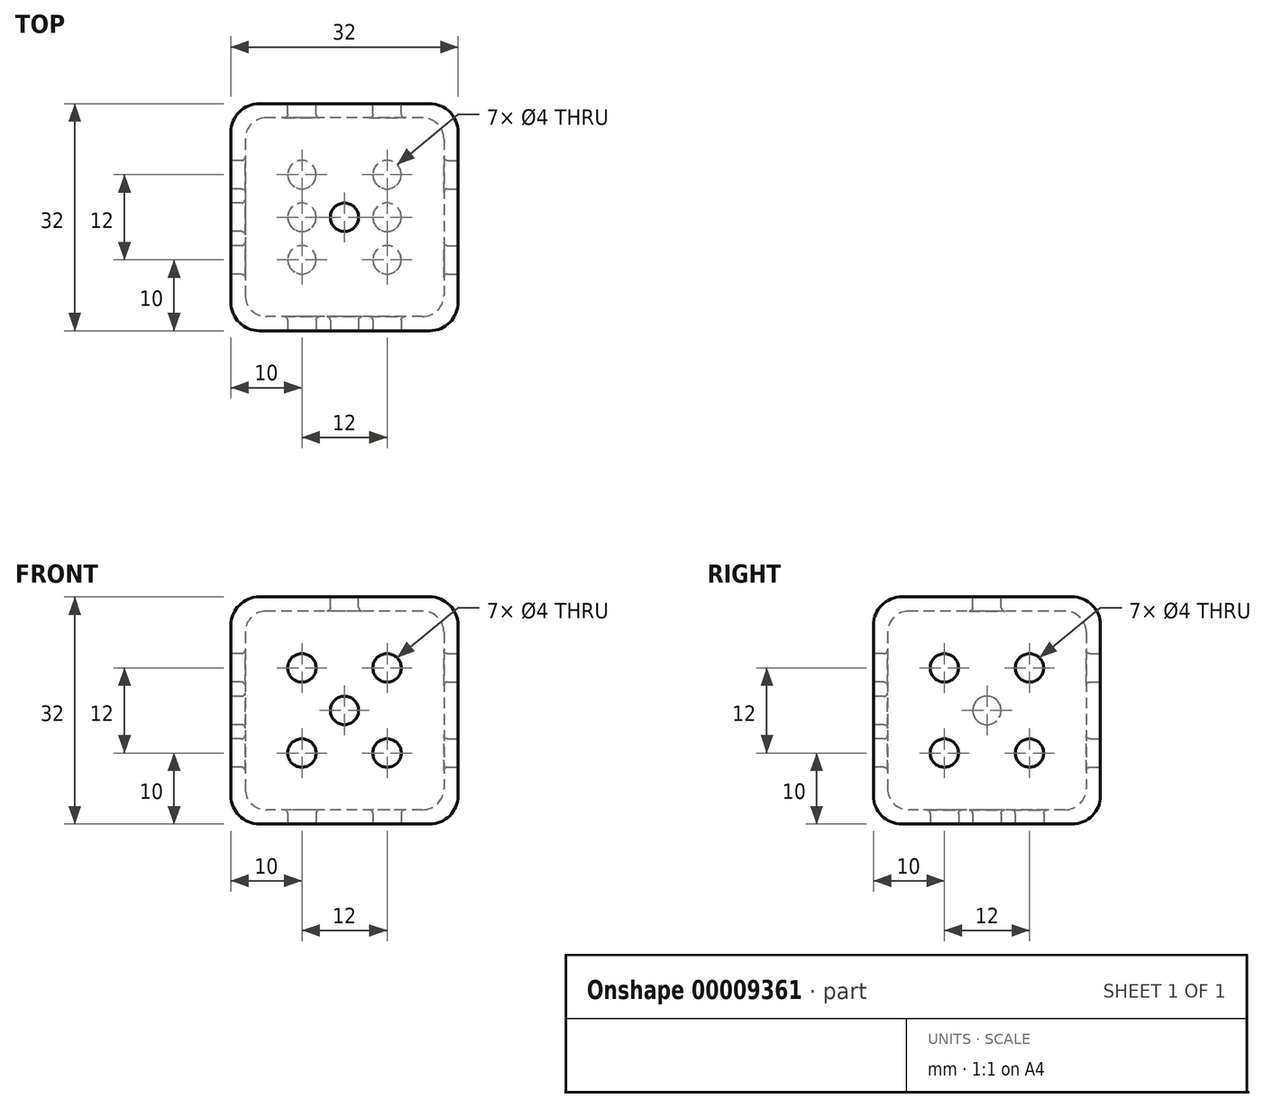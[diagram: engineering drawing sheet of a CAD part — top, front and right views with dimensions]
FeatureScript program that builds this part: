
annotation { "Feature Type Name" : "Feature", "Feature Type Description" : "" }
export const myFeature = defineFeature(function(context is Context, id is Id, definition is map)
    precondition{}
    {
        {
            var Q0;
            Q0=qCreatedBy(makeId("Top.planeOp"),FACE);
            var sketch = newSketch(context, id + "F0", { "sketchPlane" : qUnion([Q0])});
            skLineSegment(sketch, "E0.rect.bottom", {"start": v(16, 16) * mm, "end": v(-16, 16) * mm});
            skLineSegment(sketch, "E0.rect.top", {"start": v(16, -16) * mm, "end": v(-16, -16) * mm});
            skLineSegment(sketch, "E0.rect.left", {"start": v(16, 16) * mm, "end": v(16, -16) * mm});
            skLineSegment(sketch, "E0.rect.right", {"start": v(-16, 16) * mm, "end": v(-16, -16) * mm});
            skPoint(sketch, "E0.rect.middle", {"position": v(0, 0) * mm});
            skSolve(sketch);
        }
        {
            var Q0;
            Q0=makeQuery(id+"F0.imprint","IMPRINT",FACE,{"disambiguationData":[TD([[makeQuery(id+"F0.imprint","IMPRINT",EDGE,{"derivedFrom":sQuery(id+"F0.wireOp",EDGE,"E0.rect.bottom")}),1.0]])]});
            extrude(context, id + "F1", {"entities" : qUnion([Q0]), "depth" : 32 * mm});
        }
        {
            var Q0;
            Q0=qCreatedBy(makeId("Top.planeOp"),FACE);
            cPlane(context, id + "F2", {"entities" : qUnion([Q0]), "cplaneType" : CPlaneType.OFFSET, "offset" : 2 * mm, "width" : 150 * mm, "height" : 150 * mm});
        }
        {
            var Q0;
            Q0=qCreatedBy(id+"F2.planeOp",FACE);
            var sketch = newSketch(context, id + "F3", { "sketchPlane" : qUnion([Q0])});
            skLineSegment(sketch, "E1.rect.bottom", {"start": v(14, 14) * mm, "end": v(-14, 14) * mm});
            skLineSegment(sketch, "E1.rect.top", {"start": v(14, -14) * mm, "end": v(-14, -14) * mm});
            skLineSegment(sketch, "E1.rect.left", {"start": v(14, 14) * mm, "end": v(14, -14) * mm});
            skLineSegment(sketch, "E1.rect.right", {"start": v(-14, 14) * mm, "end": v(-14, -14) * mm});
            skPoint(sketch, "E1.rect.middle", {"position": v(0, 0) * mm});
            skSolve(sketch);
        }
        {
            var Q0;
            Q0 = qSketchRegion(id + "F3", true);
            extrude(context, id + "F4", {"entities" : qUnion([Q0]), "operationType" : NewBodyOperationType.REMOVE, "depth" : 28 * mm});
        }
        {
            var Q0;
            Q0=makeQuery(id+"F4.boolean.opBoolean","COPY",EDGE,{"derivedFrom":makeQuery(id+"F4.opExtrude","SWEPT_EDGE",EDGE,{"disambiguationData":[OSD([sQuery(id+"F3.wireOp",EDGE,"E1.rect.bottom"),sQuery(id+"F3.wireOp",EDGE,"E1.rect.left")])]})});
            var Q1;
            Q1=makeQuery(id+"F4.boolean.opBoolean","COPY",EDGE,{"derivedFrom":makeQuery(id+"F4.opExtrude","CAP_EDGE",EDGE,{"disambiguationData":[OSD([sQuery(id+"F3.wireOp",EDGE,"E1.rect.bottom")])],"isStart":false})});
            var Q2;
            Q2=makeQuery(id+"F4.boolean.opBoolean","COPY",EDGE,{"derivedFrom":makeQuery(id+"F4.opExtrude","CAP_EDGE",EDGE,{"disambiguationData":[OSD([sQuery(id+"F3.wireOp",EDGE,"E1.rect.left")])],"isStart":false})});
            var Q3;
            Q3=makeQuery(id+"F4.boolean.opBoolean","COPY",EDGE,{"derivedFrom":makeQuery(id+"F4.opExtrude","CAP_EDGE",EDGE,{"disambiguationData":[OSD([sQuery(id+"F3.wireOp",EDGE,"E1.rect.right")])],"isStart":false})});
            var Q4;
            Q4=makeQuery(id+"F4.boolean.opBoolean","COPY",EDGE,{"derivedFrom":makeQuery(id+"F4.opExtrude","SWEPT_EDGE",EDGE,{"disambiguationData":[OSD([sQuery(id+"F3.wireOp",EDGE,"E1.rect.bottom"),sQuery(id+"F3.wireOp",EDGE,"E1.rect.right")])]})});
            var Q5;
            Q5=makeQuery(id+"F4.boolean.opBoolean","COPY",EDGE,{"derivedFrom":makeQuery(id+"F4.opExtrude","CAP_EDGE",EDGE,{"disambiguationData":[OSD([sQuery(id+"F3.wireOp",EDGE,"E1.rect.bottom")])],"isStart":true})});
            var Q6;
            Q6=makeQuery(id+"F4.boolean.opBoolean","COPY",EDGE,{"derivedFrom":makeQuery(id+"F4.opExtrude","CAP_EDGE",EDGE,{"disambiguationData":[OSD([sQuery(id+"F3.wireOp",EDGE,"E1.rect.right")])],"isStart":true})});
            var Q7;
            Q7=makeQuery(id+"F4.boolean.opBoolean","COPY",EDGE,{"derivedFrom":makeQuery(id+"F4.opExtrude","CAP_EDGE",EDGE,{"disambiguationData":[OSD([sQuery(id+"F3.wireOp",EDGE,"E1.rect.left")])],"isStart":true})});
            var Q8;
            Q8=makeQuery(id+"F4.boolean.opBoolean","COPY",EDGE,{"derivedFrom":makeQuery(id+"F4.opExtrude","CAP_EDGE",EDGE,{"disambiguationData":[OSD([sQuery(id+"F3.wireOp",EDGE,"E1.rect.top")])],"isStart":true})});
            var Q9;
            Q9=makeQuery(id+"F4.boolean.opBoolean","COPY",EDGE,{"derivedFrom":makeQuery(id+"F4.opExtrude","SWEPT_EDGE",EDGE,{"disambiguationData":[OSD([sQuery(id+"F3.wireOp",EDGE,"E1.rect.top"),sQuery(id+"F3.wireOp",EDGE,"E1.rect.right")])]})});
            var Q10;
            Q10=makeQuery(id+"F4.boolean.opBoolean","COPY",EDGE,{"derivedFrom":makeQuery(id+"F4.opExtrude","SWEPT_EDGE",EDGE,{"disambiguationData":[OSD([sQuery(id+"F3.wireOp",EDGE,"E1.rect.top"),sQuery(id+"F3.wireOp",EDGE,"E1.rect.left")])]})});
            var Q11;
            Q11=makeQuery(id+"F4.boolean.opBoolean","COPY",EDGE,{"derivedFrom":makeQuery(id+"F4.opExtrude","CAP_EDGE",EDGE,{"disambiguationData":[OSD([sQuery(id+"F3.wireOp",EDGE,"E1.rect.top")])],"isStart":false})});
            fillet(context, id + "F5", {"entities" : qUnion([Q0, Q1, Q2, Q3, Q4, Q5, Q6, Q7, Q8, Q9, Q10, Q11]), "radius" : 3 * mm, "tangentPropagation" : true, "allowEdgeOverflow" : false});
        }
        {
            var Q0;
            Q0=makeQuery(id+"F1.opExtrude","SWEPT_EDGE",EDGE,{"disambiguationData":[OSD([sQuery(id+"F0.wireOp",EDGE,"E0.rect.bottom"),sQuery(id+"F0.wireOp",EDGE,"E0.rect.left")])]});
            var Q1;
            Q1=makeQuery(id+"F1.opExtrude","CAP_EDGE",EDGE,{"disambiguationData":[OSD([sQuery(id+"F0.wireOp",EDGE,"E0.rect.bottom")])],"isStart":false});
            var Q2;
            Q2=makeQuery(id+"F1.opExtrude","CAP_EDGE",EDGE,{"disambiguationData":[OSD([sQuery(id+"F0.wireOp",EDGE,"E0.rect.bottom")])],"isStart":true});
            var Q3;
            Q3=makeQuery(id+"F1.opExtrude","SWEPT_EDGE",EDGE,{"disambiguationData":[OSD([sQuery(id+"F0.wireOp",EDGE,"E0.rect.bottom"),sQuery(id+"F0.wireOp",EDGE,"E0.rect.right")])]});
            var Q4;
            Q4=makeQuery(id+"F1.opExtrude","CAP_EDGE",EDGE,{"disambiguationData":[OSD([sQuery(id+"F0.wireOp",EDGE,"E0.rect.right")])],"isStart":false});
            var Q5;
            Q5=makeQuery(id+"F1.opExtrude","CAP_EDGE",EDGE,{"disambiguationData":[OSD([sQuery(id+"F0.wireOp",EDGE,"E0.rect.left")])],"isStart":false});
            var Q6;
            Q6=makeQuery(id+"F1.opExtrude","CAP_EDGE",EDGE,{"disambiguationData":[OSD([sQuery(id+"F0.wireOp",EDGE,"E0.rect.left")])],"isStart":true});
            var Q7;
            Q7=makeQuery(id+"F1.opExtrude","SWEPT_EDGE",EDGE,{"disambiguationData":[OSD([sQuery(id+"F0.wireOp",EDGE,"E0.rect.top"),sQuery(id+"F0.wireOp",EDGE,"E0.rect.left")])]});
            var Q8;
            Q8=makeQuery(id+"F1.opExtrude","CAP_EDGE",EDGE,{"disambiguationData":[OSD([sQuery(id+"F0.wireOp",EDGE,"E0.rect.top")])],"isStart":false});
            var Q9;
            Q9=makeQuery(id+"F1.opExtrude","SWEPT_EDGE",EDGE,{"disambiguationData":[OSD([sQuery(id+"F0.wireOp",EDGE,"E0.rect.top"),sQuery(id+"F0.wireOp",EDGE,"E0.rect.right")])]});
            var Q10;
            Q10=makeQuery(id+"F1.opExtrude","CAP_EDGE",EDGE,{"disambiguationData":[OSD([sQuery(id+"F0.wireOp",EDGE,"E0.rect.top")])],"isStart":true});
            var Q11;
            Q11=makeQuery(id+"F1.opExtrude","CAP_EDGE",EDGE,{"disambiguationData":[OSD([sQuery(id+"F0.wireOp",EDGE,"E0.rect.right")])],"isStart":true});
            fillet(context, id + "F6", {"entities" : qUnion([Q0, Q1, Q2, Q3, Q4, Q5, Q6, Q7, Q8, Q9, Q10, Q11]), "radius" : 4 * mm, "tangentPropagation" : true, "allowEdgeOverflow" : false});
        }
        {
            var Q0;
            Q0=makeQuery(id+"F1.opExtrude","CAP_FACE",FACE,{"disambiguationData":[OSD([sQuery(id+"F0.wireOp",EDGE,"E0.rect.bottom"),sQuery(id+"F0.wireOp",EDGE,"E0.rect.top"),sQuery(id+"F0.wireOp",EDGE,"E0.rect.left"),sQuery(id+"F0.wireOp",EDGE,"E0.rect.right")])],"isStart":false});
            var sketch = newSketch(context, id + "F7", { "sketchPlane" : qUnion([Q0])});
            skCircle(sketch, "E2", {"center": v(0, 0) * mm, "radius": 2 * mm});
            skSolve(sketch);
        }
        {
            var Q0;
            Q0 = qSketchRegion(id + "F7", true);
            extrude(context, id + "F8", {"entities" : qUnion([Q0]), "operationType" : NewBodyOperationType.REMOVE, "oppositeDirection" : true, "depth" : 5 * mm});
        }
        {
            var Q0;
            Q0=makeQuery(id+"F1.opExtrude","SWEPT_FACE",FACE,{"disambiguationData":[OSD([sQuery(id+"F0.wireOp",EDGE,"E0.rect.bottom")])]});
            var sketch = newSketch(context, id + "F9", { "sketchPlane" : qUnion([Q0])});
            skLineSegment(sketch, "E3", {"start": v(12, 28) * mm, "end": v(-12, 4) * mm, "construction": true});
            skPoint(sketch, "E4", {"position": v(0, 16) * mm});
            skPoint(sketch, "E5", {"position": v(0, 28) * mm});
            skPoint(sketch, "E6", {"position": v(12, 16) * mm});
            skPoint(sketch, "E7", {"position": v(0, 4) * mm});
            skPoint(sketch, "E8", {"position": v(-12, 16) * mm});
            skLineSegment(sketch, "E9", {"start": v(0, 28) * mm, "end": v(12, 16) * mm, "construction": true});
            skLineSegment(sketch, "E10", {"start": v(-12, 16) * mm, "end": v(0, 4) * mm, "construction": true});
            skCircle(sketch, "E11", {"center": v(6, 22) * mm, "radius": 2 * mm});
            skCircle(sketch, "E12", {"center": v(-6, 10) * mm, "radius": 2 * mm});
            skSolve(sketch);
        }
        {
            var Q0;
            Q0 = qSketchRegion(id + "F9", true);
            extrude(context, id + "F10", {"entities" : qUnion([Q0]), "operationType" : NewBodyOperationType.REMOVE, "oppositeDirection" : true, "depth" : 5 * mm});
        }
        {
            var Q0;
            Q0=makeQuery(id+"F1.opExtrude","SWEPT_FACE",FACE,{"disambiguationData":[OSD([sQuery(id+"F0.wireOp",EDGE,"E0.rect.right")])]});
            var sketch = newSketch(context, id + "F11", { "sketchPlane" : qUnion([Q0])});
            skLineSegment(sketch, "E13", {"start": v(-12, 28) * mm, "end": v(12, 4) * mm, "construction": true});
            skLineSegment(sketch, "E14", {"start": v(12, 4) * mm, "end": v(0, 16) * mm, "construction": true});
            skLineSegment(sketch, "E15", {"start": v(0, 16) * mm, "end": v(-12, 28) * mm, "construction": true});
            skCircle(sketch, "E16", {"center": v(-6, 22) * mm, "radius": 2 * mm});
            skCircle(sketch, "E17", {"center": v(0, 16) * mm, "radius": 2 * mm});
            skCircle(sketch, "E18", {"center": v(6, 10) * mm, "radius": 2 * mm});
            skSolve(sketch);
        }
        {
            var Q0;
            Q0 = qSketchRegion(id + "F11", true);
            extrude(context, id + "F12", {"entities" : qUnion([Q0]), "operationType" : NewBodyOperationType.REMOVE, "oppositeDirection" : true, "depth" : 5 * mm});
        }
        {
            var Q0;
            Q0=makeQuery(id+"F1.opExtrude","SWEPT_FACE",FACE,{"disambiguationData":[OSD([sQuery(id+"F0.wireOp",EDGE,"E0.rect.left")])]});
            var sketch = newSketch(context, id + "F13", { "sketchPlane" : qUnion([Q0])});
            skLineSegment(sketch, "E19", {"start": v(-12, 16) * mm, "end": v(0, 28) * mm, "construction": true});
            skLineSegment(sketch, "E20", {"start": v(0, 28) * mm, "end": v(12, 16) * mm, "construction": true});
            skLineSegment(sketch, "E21", {"start": v(12, 16) * mm, "end": v(0, 4) * mm, "construction": true});
            skLineSegment(sketch, "E22", {"start": v(0, 4) * mm, "end": v(-12, 16) * mm, "construction": true});
            skCircle(sketch, "E23", {"center": v(-6, 10) * mm, "radius": 2 * mm});
            skCircle(sketch, "E24", {"center": v(-6, 22) * mm, "radius": 2 * mm});
            skCircle(sketch, "E25", {"center": v(6, 22) * mm, "radius": 2 * mm});
            skCircle(sketch, "E26", {"center": v(6, 10) * mm, "radius": 2 * mm});
            skSolve(sketch);
        }
        {
            var Q0;
            Q0 = qSketchRegion(id + "F13", true);
            extrude(context, id + "F14", {"entities" : qUnion([Q0]), "operationType" : NewBodyOperationType.REMOVE, "oppositeDirection" : true, "depth" : 5 * mm});
        }
        {
            var Q0;
            Q0=makeQuery(id+"F1.opExtrude","SWEPT_FACE",FACE,{"disambiguationData":[OSD([sQuery(id+"F0.wireOp",EDGE,"E0.rect.top")])]});
            var sketch = newSketch(context, id + "F15", { "sketchPlane" : qUnion([Q0])});
            skLineSegment(sketch, "E27", {"start": v(0, 28) * mm, "end": v(12, 16) * mm, "construction": true});
            skLineSegment(sketch, "E28", {"start": v(12, 16) * mm, "end": v(0, 4) * mm, "construction": true});
            skLineSegment(sketch, "E29", {"start": v(0, 4) * mm, "end": v(-12, 16) * mm, "construction": true});
            skLineSegment(sketch, "E30", {"start": v(-12, 16) * mm, "end": v(0, 28) * mm, "construction": true});
            skLineSegment(sketch, "E31", {"start": v(-12, 16) * mm, "end": v(12, 16) * mm, "construction": true});
            skCircle(sketch, "E32", {"center": v(-6, 22) * mm, "radius": 2 * mm});
            skCircle(sketch, "E33", {"center": v(6, 22) * mm, "radius": 2 * mm});
            skCircle(sketch, "E34", {"center": v(6, 10) * mm, "radius": 2 * mm});
            skCircle(sketch, "E35", {"center": v(-6, 10) * mm, "radius": 2 * mm});
            skCircle(sketch, "E36", {"center": v(0, 16) * mm, "radius": 2 * mm});
            skSolve(sketch);
        }
        {
            var Q0;
            Q0 = qSketchRegion(id + "F15", true);
            extrude(context, id + "F16", {"entities" : qUnion([Q0]), "operationType" : NewBodyOperationType.REMOVE, "oppositeDirection" : true, "depth" : 5 * mm});
        }
        {
            var Q0;
            Q0=makeQuery(id+"F1.opExtrude","CAP_FACE",FACE,{"disambiguationData":[OSD([sQuery(id+"F0.wireOp",EDGE,"E0.rect.bottom"),sQuery(id+"F0.wireOp",EDGE,"E0.rect.top"),sQuery(id+"F0.wireOp",EDGE,"E0.rect.left"),sQuery(id+"F0.wireOp",EDGE,"E0.rect.right")])],"isStart":true});
            var sketch = newSketch(context, id + "F17", { "sketchPlane" : qUnion([Q0])});
            skLineSegment(sketch, "E37", {"start": v(0, 12) * mm, "end": v(-12, 0) * mm, "construction": true});
            skLineSegment(sketch, "E38", {"start": v(-12, 0) * mm, "end": v(0, -12) * mm, "construction": true});
            skLineSegment(sketch, "E39", {"start": v(0, -12) * mm, "end": v(12, 0) * mm, "construction": true});
            skLineSegment(sketch, "E40", {"start": v(12, 0) * mm, "end": v(0, 12) * mm, "construction": true});
            skLineSegment(sketch, "E41", {"start": v(6, 6) * mm, "end": v(6, -6) * mm, "construction": true});
            skLineSegment(sketch, "E42", {"start": v(6, -6) * mm, "end": v(-6, -6) * mm, "construction": true});
            skLineSegment(sketch, "E43", {"start": v(-6, -6) * mm, "end": v(-6, 6) * mm, "construction": true});
            skLineSegment(sketch, "E44", {"start": v(-6, 6) * mm, "end": v(6, 6) * mm, "construction": true});
            skCircle(sketch, "E45", {"center": v(-6, 6) * mm, "radius": 2 * mm});
            skCircle(sketch, "E46", {"center": v(-6, 0) * mm, "radius": 2 * mm});
            skCircle(sketch, "E47", {"center": v(-6, -6) * mm, "radius": 2 * mm});
            skCircle(sketch, "E48", {"center": v(6, -6) * mm, "radius": 2 * mm});
            skCircle(sketch, "E49", {"center": v(6, 0) * mm, "radius": 2 * mm});
            skCircle(sketch, "E50", {"center": v(6, 6) * mm, "radius": 2 * mm});
            skSolve(sketch);
        }
        {
            var Q0;
            Q0 = qSketchRegion(id + "F17", true);
            extrude(context, id + "F18", {"entities" : qUnion([Q0]), "operationType" : NewBodyOperationType.REMOVE, "oppositeDirection" : true, "depth" : 5 * mm});
        }
        {
            var Q0;
            Q0=makeQuery(id+"F8.boolean.opBoolean","COPY",EDGE,{"derivedFrom":makeQuery(id+"F8.opExtrude","CAP_EDGE",EDGE,{"disambiguationData":[OSD([sQuery(id+"F7.wireOp",EDGE,"E2")])],"isStart":true})});
            var Q1;
            Q1=makeQuery(id+"F8.boolean.opBoolean","INTERSECT",EDGE,{"derivedFrom":[makeQuery(id+"F4.boolean.opBoolean","COPY",FACE,{"derivedFrom":makeQuery(id+"F4.opExtrude","CAP_FACE",FACE,{"disambiguationData":[OSD([sQuery(id+"F3.wireOp",EDGE,"E1.rect.bottom"),sQuery(id+"F3.wireOp",EDGE,"E1.rect.top"),sQuery(id+"F3.wireOp",EDGE,"E1.rect.left"),sQuery(id+"F3.wireOp",EDGE,"E1.rect.right")])],"isStart":false})}),makeQuery(id+"F8.opExtrude","SWEPT_FACE",FACE,{"disambiguationData":[OSD([sQuery(id+"F7.wireOp",EDGE,"E2")])]})]});
            var Q2;
            Q2=makeQuery(id+"F10.boolean.opBoolean","COPY",EDGE,{"derivedFrom":makeQuery(id+"F10.opExtrude","CAP_EDGE",EDGE,{"disambiguationData":[OSD([sQuery(id+"F9.wireOp",EDGE,"E11")])],"isStart":true})});
            var Q3;
            Q3=makeQuery(id+"F10.boolean.opBoolean","COPY",EDGE,{"derivedFrom":makeQuery(id+"F10.opExtrude","CAP_EDGE",EDGE,{"disambiguationData":[OSD([sQuery(id+"F9.wireOp",EDGE,"E12")])],"isStart":true})});
            var Q4;
            Q4=makeQuery(id+"F10.boolean.opBoolean","INTERSECT",EDGE,{"derivedFrom":[makeQuery(id+"F4.boolean.opBoolean","COPY",FACE,{"derivedFrom":makeQuery(id+"F4.opExtrude","SWEPT_FACE",FACE,{"disambiguationData":[OSD([sQuery(id+"F3.wireOp",EDGE,"E1.rect.bottom")])]})}),makeQuery(id+"F10.opExtrude","SWEPT_FACE",FACE,{"disambiguationData":[OSD([sQuery(id+"F9.wireOp",EDGE,"E11")])]})]});
            var Q5;
            Q5=makeQuery(id+"F10.boolean.opBoolean","INTERSECT",EDGE,{"derivedFrom":[makeQuery(id+"F4.boolean.opBoolean","COPY",FACE,{"derivedFrom":makeQuery(id+"F4.opExtrude","SWEPT_FACE",FACE,{"disambiguationData":[OSD([sQuery(id+"F3.wireOp",EDGE,"E1.rect.bottom")])]})}),makeQuery(id+"F10.opExtrude","SWEPT_FACE",FACE,{"disambiguationData":[OSD([sQuery(id+"F9.wireOp",EDGE,"E12")])]})]});
            var Q6;
            Q6=makeQuery(id+"F12.boolean.opBoolean","INTERSECT",EDGE,{"derivedFrom":[makeQuery(id+"F4.boolean.opBoolean","COPY",FACE,{"derivedFrom":makeQuery(id+"F4.opExtrude","SWEPT_FACE",FACE,{"disambiguationData":[OSD([sQuery(id+"F3.wireOp",EDGE,"E1.rect.right")])]})}),makeQuery(id+"F12.opExtrude","SWEPT_FACE",FACE,{"disambiguationData":[OSD([sQuery(id+"F11.wireOp",EDGE,"E16")])]})]});
            var Q7;
            Q7=makeQuery(id+"F12.boolean.opBoolean","COPY",EDGE,{"derivedFrom":makeQuery(id+"F12.opExtrude","CAP_EDGE",EDGE,{"disambiguationData":[OSD([sQuery(id+"F11.wireOp",EDGE,"E16")])],"isStart":true})});
            var Q8;
            Q8=makeQuery(id+"F12.boolean.opBoolean","INTERSECT",EDGE,{"derivedFrom":[makeQuery(id+"F4.boolean.opBoolean","COPY",FACE,{"derivedFrom":makeQuery(id+"F4.opExtrude","SWEPT_FACE",FACE,{"disambiguationData":[OSD([sQuery(id+"F3.wireOp",EDGE,"E1.rect.right")])]})}),makeQuery(id+"F12.opExtrude","SWEPT_FACE",FACE,{"disambiguationData":[OSD([sQuery(id+"F11.wireOp",EDGE,"E17")])]})]});
            var Q9;
            Q9=makeQuery(id+"F12.boolean.opBoolean","COPY",EDGE,{"derivedFrom":makeQuery(id+"F12.opExtrude","CAP_EDGE",EDGE,{"disambiguationData":[OSD([sQuery(id+"F11.wireOp",EDGE,"E17")])],"isStart":true})});
            var Q10;
            Q10=makeQuery(id+"F12.boolean.opBoolean","INTERSECT",EDGE,{"derivedFrom":[makeQuery(id+"F4.boolean.opBoolean","COPY",FACE,{"derivedFrom":makeQuery(id+"F4.opExtrude","SWEPT_FACE",FACE,{"disambiguationData":[OSD([sQuery(id+"F3.wireOp",EDGE,"E1.rect.right")])]})}),makeQuery(id+"F12.opExtrude","SWEPT_FACE",FACE,{"disambiguationData":[OSD([sQuery(id+"F11.wireOp",EDGE,"E18")])]})]});
            var Q11;
            Q11=makeQuery(id+"F12.boolean.opBoolean","COPY",EDGE,{"derivedFrom":makeQuery(id+"F12.opExtrude","CAP_EDGE",EDGE,{"disambiguationData":[OSD([sQuery(id+"F11.wireOp",EDGE,"E18")])],"isStart":true})});
            var Q12;
            Q12=makeQuery(id+"F14.boolean.opBoolean","INTERSECT",EDGE,{"derivedFrom":[makeQuery(id+"F4.boolean.opBoolean","COPY",FACE,{"derivedFrom":makeQuery(id+"F4.opExtrude","SWEPT_FACE",FACE,{"disambiguationData":[OSD([sQuery(id+"F3.wireOp",EDGE,"E1.rect.left")])]})}),makeQuery(id+"F14.opExtrude","SWEPT_FACE",FACE,{"disambiguationData":[OSD([sQuery(id+"F13.wireOp",EDGE,"E24")])]})]});
            var Q13;
            Q13=makeQuery(id+"F14.boolean.opBoolean","COPY",EDGE,{"derivedFrom":makeQuery(id+"F14.opExtrude","CAP_EDGE",EDGE,{"disambiguationData":[OSD([sQuery(id+"F13.wireOp",EDGE,"E24")])],"isStart":true})});
            var Q14;
            Q14=makeQuery(id+"F14.boolean.opBoolean","INTERSECT",EDGE,{"derivedFrom":[makeQuery(id+"F4.boolean.opBoolean","COPY",FACE,{"derivedFrom":makeQuery(id+"F4.opExtrude","SWEPT_FACE",FACE,{"disambiguationData":[OSD([sQuery(id+"F3.wireOp",EDGE,"E1.rect.left")])]})}),makeQuery(id+"F14.opExtrude","SWEPT_FACE",FACE,{"disambiguationData":[OSD([sQuery(id+"F13.wireOp",EDGE,"E25")])]})]});
            var Q15;
            Q15=makeQuery(id+"F14.boolean.opBoolean","COPY",EDGE,{"derivedFrom":makeQuery(id+"F14.opExtrude","CAP_EDGE",EDGE,{"disambiguationData":[OSD([sQuery(id+"F13.wireOp",EDGE,"E25")])],"isStart":true})});
            var Q16;
            Q16=makeQuery(id+"F14.boolean.opBoolean","INTERSECT",EDGE,{"derivedFrom":[makeQuery(id+"F4.boolean.opBoolean","COPY",FACE,{"derivedFrom":makeQuery(id+"F4.opExtrude","SWEPT_FACE",FACE,{"disambiguationData":[OSD([sQuery(id+"F3.wireOp",EDGE,"E1.rect.left")])]})}),makeQuery(id+"F14.opExtrude","SWEPT_FACE",FACE,{"disambiguationData":[OSD([sQuery(id+"F13.wireOp",EDGE,"E26")])]})]});
            var Q17;
            Q17=makeQuery(id+"F14.boolean.opBoolean","COPY",EDGE,{"derivedFrom":makeQuery(id+"F14.opExtrude","CAP_EDGE",EDGE,{"disambiguationData":[OSD([sQuery(id+"F13.wireOp",EDGE,"E26")])],"isStart":true})});
            var Q18;
            Q18=makeQuery(id+"F14.boolean.opBoolean","INTERSECT",EDGE,{"derivedFrom":[makeQuery(id+"F4.boolean.opBoolean","COPY",FACE,{"derivedFrom":makeQuery(id+"F4.opExtrude","SWEPT_FACE",FACE,{"disambiguationData":[OSD([sQuery(id+"F3.wireOp",EDGE,"E1.rect.left")])]})}),makeQuery(id+"F14.opExtrude","SWEPT_FACE",FACE,{"disambiguationData":[OSD([sQuery(id+"F13.wireOp",EDGE,"E23")])]})]});
            var Q19;
            Q19=makeQuery(id+"F14.boolean.opBoolean","COPY",EDGE,{"derivedFrom":makeQuery(id+"F14.opExtrude","CAP_EDGE",EDGE,{"disambiguationData":[OSD([sQuery(id+"F13.wireOp",EDGE,"E23")])],"isStart":true})});
            var Q20;
            Q20=makeQuery(id+"F16.boolean.opBoolean","INTERSECT",EDGE,{"derivedFrom":[makeQuery(id+"F4.boolean.opBoolean","COPY",FACE,{"derivedFrom":makeQuery(id+"F4.opExtrude","SWEPT_FACE",FACE,{"disambiguationData":[OSD([sQuery(id+"F3.wireOp",EDGE,"E1.rect.top")])]})}),makeQuery(id+"F16.opExtrude","SWEPT_FACE",FACE,{"disambiguationData":[OSD([sQuery(id+"F15.wireOp",EDGE,"E33")])]})]});
            var Q21;
            Q21=makeQuery(id+"F16.boolean.opBoolean","COPY",EDGE,{"derivedFrom":makeQuery(id+"F16.opExtrude","CAP_EDGE",EDGE,{"disambiguationData":[OSD([sQuery(id+"F15.wireOp",EDGE,"E33")])],"isStart":true})});
            var Q22;
            Q22=makeQuery(id+"F16.boolean.opBoolean","INTERSECT",EDGE,{"derivedFrom":[makeQuery(id+"F4.boolean.opBoolean","COPY",FACE,{"derivedFrom":makeQuery(id+"F4.opExtrude","SWEPT_FACE",FACE,{"disambiguationData":[OSD([sQuery(id+"F3.wireOp",EDGE,"E1.rect.top")])]})}),makeQuery(id+"F16.opExtrude","SWEPT_FACE",FACE,{"disambiguationData":[OSD([sQuery(id+"F15.wireOp",EDGE,"E32")])]})]});
            var Q23;
            Q23=makeQuery(id+"F16.boolean.opBoolean","COPY",EDGE,{"derivedFrom":makeQuery(id+"F16.opExtrude","CAP_EDGE",EDGE,{"disambiguationData":[OSD([sQuery(id+"F15.wireOp",EDGE,"E32")])],"isStart":true})});
            var Q24;
            Q24=makeQuery(id+"F16.boolean.opBoolean","INTERSECT",EDGE,{"derivedFrom":[makeQuery(id+"F4.boolean.opBoolean","COPY",FACE,{"derivedFrom":makeQuery(id+"F4.opExtrude","SWEPT_FACE",FACE,{"disambiguationData":[OSD([sQuery(id+"F3.wireOp",EDGE,"E1.rect.top")])]})}),makeQuery(id+"F16.opExtrude","SWEPT_FACE",FACE,{"disambiguationData":[OSD([sQuery(id+"F15.wireOp",EDGE,"E34")])]})]});
            var Q25;
            Q25=makeQuery(id+"F16.boolean.opBoolean","COPY",EDGE,{"derivedFrom":makeQuery(id+"F16.opExtrude","CAP_EDGE",EDGE,{"disambiguationData":[OSD([sQuery(id+"F15.wireOp",EDGE,"E34")])],"isStart":true})});
            var Q26;
            Q26=makeQuery(id+"F16.boolean.opBoolean","INTERSECT",EDGE,{"derivedFrom":[makeQuery(id+"F4.boolean.opBoolean","COPY",FACE,{"derivedFrom":makeQuery(id+"F4.opExtrude","SWEPT_FACE",FACE,{"disambiguationData":[OSD([sQuery(id+"F3.wireOp",EDGE,"E1.rect.top")])]})}),makeQuery(id+"F16.opExtrude","SWEPT_FACE",FACE,{"disambiguationData":[OSD([sQuery(id+"F15.wireOp",EDGE,"E35")])]})]});
            var Q27;
            Q27=makeQuery(id+"F16.boolean.opBoolean","COPY",EDGE,{"derivedFrom":makeQuery(id+"F16.opExtrude","CAP_EDGE",EDGE,{"disambiguationData":[OSD([sQuery(id+"F15.wireOp",EDGE,"E35")])],"isStart":true})});
            var Q28;
            Q28=makeQuery(id+"F16.boolean.opBoolean","INTERSECT",EDGE,{"derivedFrom":[makeQuery(id+"F4.boolean.opBoolean","COPY",FACE,{"derivedFrom":makeQuery(id+"F4.opExtrude","SWEPT_FACE",FACE,{"disambiguationData":[OSD([sQuery(id+"F3.wireOp",EDGE,"E1.rect.top")])]})}),makeQuery(id+"F16.opExtrude","SWEPT_FACE",FACE,{"disambiguationData":[OSD([sQuery(id+"F15.wireOp",EDGE,"E36")])]})]});
            var Q29;
            Q29=makeQuery(id+"F16.boolean.opBoolean","COPY",EDGE,{"derivedFrom":makeQuery(id+"F16.opExtrude","CAP_EDGE",EDGE,{"disambiguationData":[OSD([sQuery(id+"F15.wireOp",EDGE,"E36")])],"isStart":true})});
            var Q30;
            Q30=makeQuery(id+"F18.boolean.opBoolean","INTERSECT",EDGE,{"derivedFrom":[makeQuery(id+"F4.boolean.opBoolean","COPY",FACE,{"derivedFrom":makeQuery(id+"F4.opExtrude","CAP_FACE",FACE,{"disambiguationData":[OSD([sQuery(id+"F3.wireOp",EDGE,"E1.rect.bottom"),sQuery(id+"F3.wireOp",EDGE,"E1.rect.top"),sQuery(id+"F3.wireOp",EDGE,"E1.rect.left"),sQuery(id+"F3.wireOp",EDGE,"E1.rect.right")])],"isStart":true})}),makeQuery(id+"F18.opExtrude","SWEPT_FACE",FACE,{"disambiguationData":[OSD([sQuery(id+"F17.wireOp",EDGE,"E50")])]})]});
            var Q31;
            Q31=makeQuery(id+"F18.boolean.opBoolean","COPY",EDGE,{"derivedFrom":makeQuery(id+"F18.opExtrude","CAP_EDGE",EDGE,{"disambiguationData":[OSD([sQuery(id+"F17.wireOp",EDGE,"E50")])],"isStart":true})});
            var Q32;
            Q32=makeQuery(id+"F18.boolean.opBoolean","INTERSECT",EDGE,{"derivedFrom":[makeQuery(id+"F4.boolean.opBoolean","COPY",FACE,{"derivedFrom":makeQuery(id+"F4.opExtrude","CAP_FACE",FACE,{"disambiguationData":[OSD([sQuery(id+"F3.wireOp",EDGE,"E1.rect.bottom"),sQuery(id+"F3.wireOp",EDGE,"E1.rect.top"),sQuery(id+"F3.wireOp",EDGE,"E1.rect.left"),sQuery(id+"F3.wireOp",EDGE,"E1.rect.right")])],"isStart":true})}),makeQuery(id+"F18.opExtrude","SWEPT_FACE",FACE,{"disambiguationData":[OSD([sQuery(id+"F17.wireOp",EDGE,"E49")])]})]});
            var Q33;
            Q33=makeQuery(id+"F18.boolean.opBoolean","COPY",EDGE,{"derivedFrom":makeQuery(id+"F18.opExtrude","CAP_EDGE",EDGE,{"disambiguationData":[OSD([sQuery(id+"F17.wireOp",EDGE,"E49")])],"isStart":true})});
            var Q34;
            Q34=makeQuery(id+"F18.boolean.opBoolean","INTERSECT",EDGE,{"derivedFrom":[makeQuery(id+"F4.boolean.opBoolean","COPY",FACE,{"derivedFrom":makeQuery(id+"F4.opExtrude","CAP_FACE",FACE,{"disambiguationData":[OSD([sQuery(id+"F3.wireOp",EDGE,"E1.rect.bottom"),sQuery(id+"F3.wireOp",EDGE,"E1.rect.top"),sQuery(id+"F3.wireOp",EDGE,"E1.rect.left"),sQuery(id+"F3.wireOp",EDGE,"E1.rect.right")])],"isStart":true})}),makeQuery(id+"F18.opExtrude","SWEPT_FACE",FACE,{"disambiguationData":[OSD([sQuery(id+"F17.wireOp",EDGE,"E48")])]})]});
            var Q35;
            Q35=makeQuery(id+"F18.boolean.opBoolean","COPY",EDGE,{"derivedFrom":makeQuery(id+"F18.opExtrude","CAP_EDGE",EDGE,{"disambiguationData":[OSD([sQuery(id+"F17.wireOp",EDGE,"E48")])],"isStart":true})});
            var Q36;
            Q36=makeQuery(id+"F18.boolean.opBoolean","INTERSECT",EDGE,{"derivedFrom":[makeQuery(id+"F4.boolean.opBoolean","COPY",FACE,{"derivedFrom":makeQuery(id+"F4.opExtrude","CAP_FACE",FACE,{"disambiguationData":[OSD([sQuery(id+"F3.wireOp",EDGE,"E1.rect.bottom"),sQuery(id+"F3.wireOp",EDGE,"E1.rect.top"),sQuery(id+"F3.wireOp",EDGE,"E1.rect.left"),sQuery(id+"F3.wireOp",EDGE,"E1.rect.right")])],"isStart":true})}),makeQuery(id+"F18.opExtrude","SWEPT_FACE",FACE,{"disambiguationData":[OSD([sQuery(id+"F17.wireOp",EDGE,"E45")])]})]});
            var Q37;
            Q37=makeQuery(id+"F18.boolean.opBoolean","COPY",EDGE,{"derivedFrom":makeQuery(id+"F18.opExtrude","CAP_EDGE",EDGE,{"disambiguationData":[OSD([sQuery(id+"F17.wireOp",EDGE,"E45")])],"isStart":true})});
            var Q38;
            Q38=makeQuery(id+"F18.boolean.opBoolean","INTERSECT",EDGE,{"derivedFrom":[makeQuery(id+"F4.boolean.opBoolean","COPY",FACE,{"derivedFrom":makeQuery(id+"F4.opExtrude","CAP_FACE",FACE,{"disambiguationData":[OSD([sQuery(id+"F3.wireOp",EDGE,"E1.rect.bottom"),sQuery(id+"F3.wireOp",EDGE,"E1.rect.top"),sQuery(id+"F3.wireOp",EDGE,"E1.rect.left"),sQuery(id+"F3.wireOp",EDGE,"E1.rect.right")])],"isStart":true})}),makeQuery(id+"F18.opExtrude","SWEPT_FACE",FACE,{"disambiguationData":[OSD([sQuery(id+"F17.wireOp",EDGE,"E46")])]})]});
            var Q39;
            Q39=makeQuery(id+"F18.boolean.opBoolean","COPY",EDGE,{"derivedFrom":makeQuery(id+"F18.opExtrude","CAP_EDGE",EDGE,{"disambiguationData":[OSD([sQuery(id+"F17.wireOp",EDGE,"E46")])],"isStart":true})});
            var Q40;
            Q40=makeQuery(id+"F18.boolean.opBoolean","INTERSECT",EDGE,{"derivedFrom":[makeQuery(id+"F4.boolean.opBoolean","COPY",FACE,{"derivedFrom":makeQuery(id+"F4.opExtrude","CAP_FACE",FACE,{"disambiguationData":[OSD([sQuery(id+"F3.wireOp",EDGE,"E1.rect.bottom"),sQuery(id+"F3.wireOp",EDGE,"E1.rect.top"),sQuery(id+"F3.wireOp",EDGE,"E1.rect.left"),sQuery(id+"F3.wireOp",EDGE,"E1.rect.right")])],"isStart":true})}),makeQuery(id+"F18.opExtrude","SWEPT_FACE",FACE,{"disambiguationData":[OSD([sQuery(id+"F17.wireOp",EDGE,"E47")])]})]});
            var Q41;
            Q41=makeQuery(id+"F18.boolean.opBoolean","COPY",EDGE,{"derivedFrom":makeQuery(id+"F18.opExtrude","CAP_EDGE",EDGE,{"disambiguationData":[OSD([sQuery(id+"F17.wireOp",EDGE,"E47")])],"isStart":true})});
            fillet(context, id + "F19", {"entities" : qUnion([Q0, Q1, Q2, Q3, Q4, Q5, Q6, Q7, Q8, Q9, Q10, Q11, Q12, Q13, Q14, Q15, Q16, Q17, Q18, Q19, Q20, Q21, Q22, Q23, Q24, Q25, Q26, Q27, Q28, Q29, Q30, Q31, Q32, Q33, Q34, Q35, Q36, Q37, Q38, Q39, Q40, Q41]), "radius" : 0.5 * mm, "tangentPropagation" : true, "allowEdgeOverflow" : false});
        }
    });
